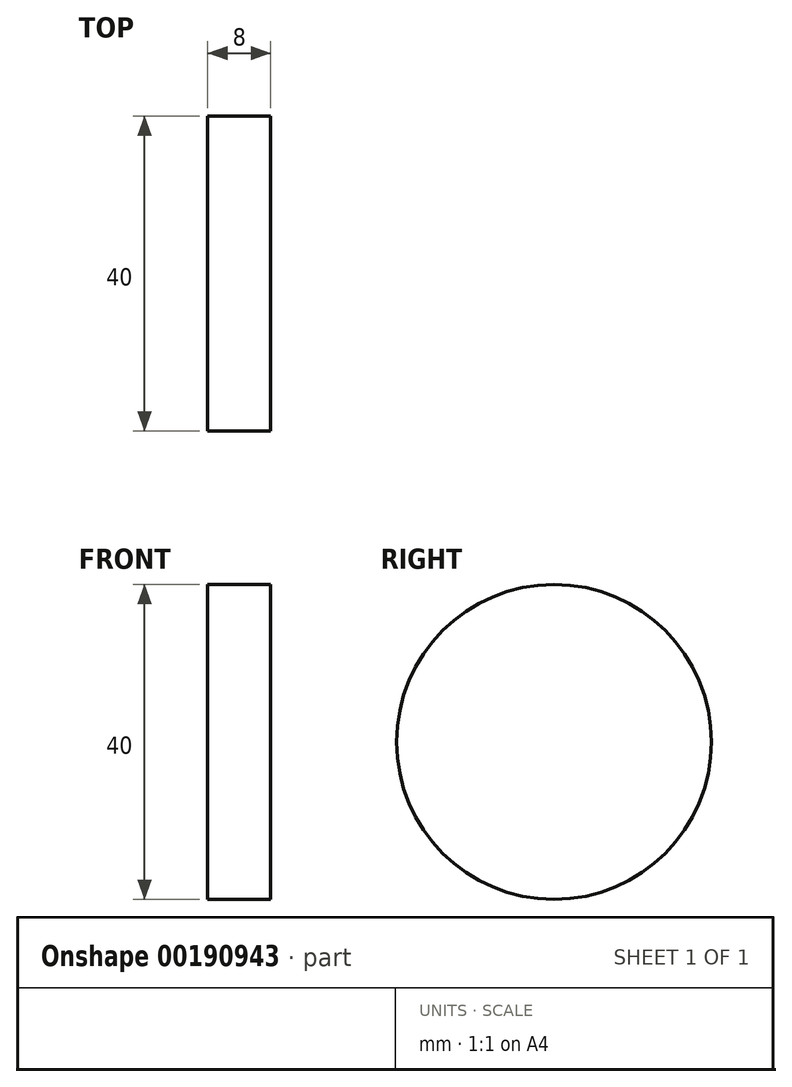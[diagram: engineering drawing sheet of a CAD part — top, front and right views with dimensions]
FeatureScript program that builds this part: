
annotation { "Feature Type Name" : "Feature", "Feature Type Description" : "" }
export const myFeature = defineFeature(function(context is Context, id is Id, definition is map)
    precondition{}
    {
        {
            var Q0;
            Q0=qCreatedBy(makeId("Right.planeOp"),FACE);
            var sketch = newSketch(context, id + "F0", { "sketchPlane" : qUnion([Q0])});
            skCircle(sketch, "E0", {"center": v(0, 0) * mm, "radius": 20 * mm});
            skSolve(sketch);
        }
        {
            var Q0;
            Q0 = qSketchRegion(id + "F0", true);
            extrude(context, id + "F1", {"entities" : qUnion([Q0]), "depth" : 8 * mm, "symmetric" : true});
        }
    });
